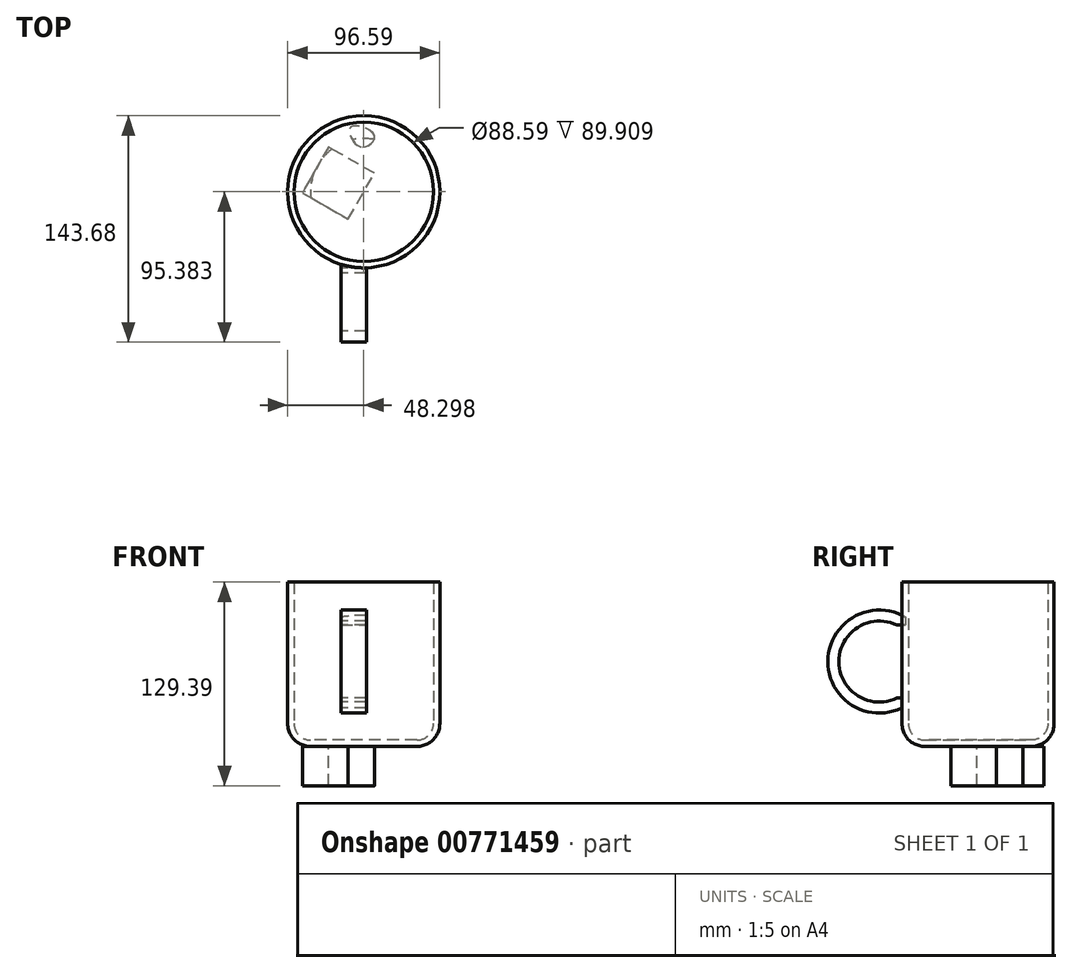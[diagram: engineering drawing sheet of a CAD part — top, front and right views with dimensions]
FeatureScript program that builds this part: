
annotation { "Feature Type Name" : "Feature", "Feature Type Description" : "" }
export const myFeature = defineFeature(function(context is Context, id is Id, definition is map)
    precondition{}
    {
        {
            var Q0;
            Q0=qCreatedBy(makeId("Top.planeOp"),FACE);
            var sketch = newSketch(context, id + "F0", { "sketchPlane" : qUnion([Q0])});
            skCircle(sketch, "E0", {"center": v(6.4, 6.86) * mm, "radius": 48.3 * mm});
            skPoint(sketch, "E0.first.point", {"position": v(-41.8, 3.96) * mm});
            skPoint(sketch, "E0.second.point", {"position": v(51.82, 23.26) * mm});
            skPoint(sketch, "E0.third.point", {"position": v(-33.95, -19.67) * mm});
            skSolve(sketch);
        }
        {
            var Q0;
            Q0=makeQuery(id+"F0.imprint","IMPRINT",FACE,{"disambiguationData":[TD([[makeQuery(id+"F0.imprint","IMPRINT",EDGE,{"derivedFrom":sQuery(id+"F0.wireOp",EDGE,"E0")}),1.0]])]});
            extrude(context, id + "F1", {"entities" : qUnion([Q0]), "depth" : 104.4 * mm, "offsetDistance" : 25.4 * mm});
        }
        {
            var Q0;
            Q0=makeQuery(id+"F1.opExtrude","CAP_EDGE",EDGE,{"disambiguationData":[OSD([sQuery(id+"F0.wireOp",EDGE,"E0")])],"isStart":true});
            fillet(context, id + "F2", {"entities" : qUnion([Q0]), "radius" : 14.5 * mm, "tangentPropagation" : true, "allowEdgeOverflow" : false});
        }
        {
            var Q0;
            Q0=makeQuery(id+"F1.opExtrude","CAP_FACE",FACE,{"disambiguationData":[OSD([sQuery(id+"F0.wireOp",EDGE,"E0")])],"isStart":false});
            shell(context, id + "F3", {"entities" : qUnion([Q0]), "thickness" : 4 * mm});
        }
        {
            var Q0;
            Q0=makeQuery(id+"F1.opExtrude","CAP_FACE",FACE,{"disambiguationData":[OSD([sQuery(id+"F0.wireOp",EDGE,"E0")])],"isStart":true});
            var sketch = newSketch(context, id + "F4", { "sketchPlane" : qUnion([Q0])});
            skCircle(sketch, "E1.cCircle", {"center": v(-9.67, -12.42) * mm, "radius": 16.77 * mm, "construction": true});
            skLineSegment(sketch, "E1.0", {"start": v(-15.9, -35.3) * mm, "end": v(-32.55, -6.2) * mm});
            skLineSegment(sketch, "E1.1", {"start": v(-32.55, -6.2) * mm, "end": v(-3.44, 10.46) * mm});
            skLineSegment(sketch, "E1.2", {"start": v(-3.44, 10.46) * mm, "end": v(13.2, -18.65) * mm});
            skLineSegment(sketch, "E1.3", {"start": v(13.2, -18.65) * mm, "end": v(-15.9, -35.3) * mm});
            skPoint(sketch, "E1.0.midPoint", {"position": v(-24.22, -20.75) * mm});
            skPoint(sketch, "E2.1.internal.snap0", {"position": v(-1.35, -26.98) * mm});
            skPoint(sketch, "E2.2.internal.snap0", {"position": v(-1.35, -26.98) * mm});
            skFitSpline(sketch, "E2", {"points": [v(13.2, -42.52) * mm, v(-1.35, -48.37) * mm, v(-1.35, -40.85) * mm, v(6.35, -35.3) * mm, v(13.2, -42.52) * mm]});
            skSolve(sketch);
        }
        {
            var Q0;
            Q0=qCreatedBy(makeId("Right.planeOp"),FACE);
            var sketch = newSketch(context, id + "F5", { "sketchPlane" : qUnion([Q0])});
            skArc(sketch, "E3", {"start": v(-38.84, 81.84) * mm, "mid": v(-88.48, 55.41) * mm, "end": v(-41.58, 24.4) * mm});
            skArc(sketch, "E4.0", {"start": v(-44.62, 77.02) * mm, "mid": v(-81.52, 53.86) * mm, "end": v(-44.62, 30.7) * mm});
            skLineSegment(sketch, "E5", {"start": v(-44.62, 77.02) * mm, "end": v(-38.84, 77.02) * mm});
            skLineSegment(sketch, "E6", {"start": v(-44.62, 30.7) * mm, "end": v(-41.58, 30.77) * mm});
            skLineSegment(sketch, "E7", {"start": v(-41.58, 30.77) * mm, "end": v(-41.58, 24.4) * mm});
            skLineSegment(sketch, "E8", {"start": v(-38.84, 81.84) * mm, "end": v(-38.84, 77.02) * mm});
            skPoint(sketch, "E9.orphan", {"position": v(-41.58, 83.32) * mm});
            skSolve(sketch);
        }
        {
            var Q0;
            Q0 = qSketchRegion(id + "F5", true);
            extrude(context, id + "F6", {"entities" : qUnion([Q0]), "operationType" : NewBodyOperationType.ADD, "endBound" : BoundingType.SYMMETRIC, "depth" : 16.2 * mm, "offsetDistance" : 25 * mm});
        }
        {
            var Q0;
            Q0 = qSketchRegion(id + "F4", true);
            extrude(context, id + "F7", {"entities" : qUnion([Q0]), "operationType" : NewBodyOperationType.ADD, "depth" : 25 * mm, "offsetDistance" : 25 * mm});
        }
    });
